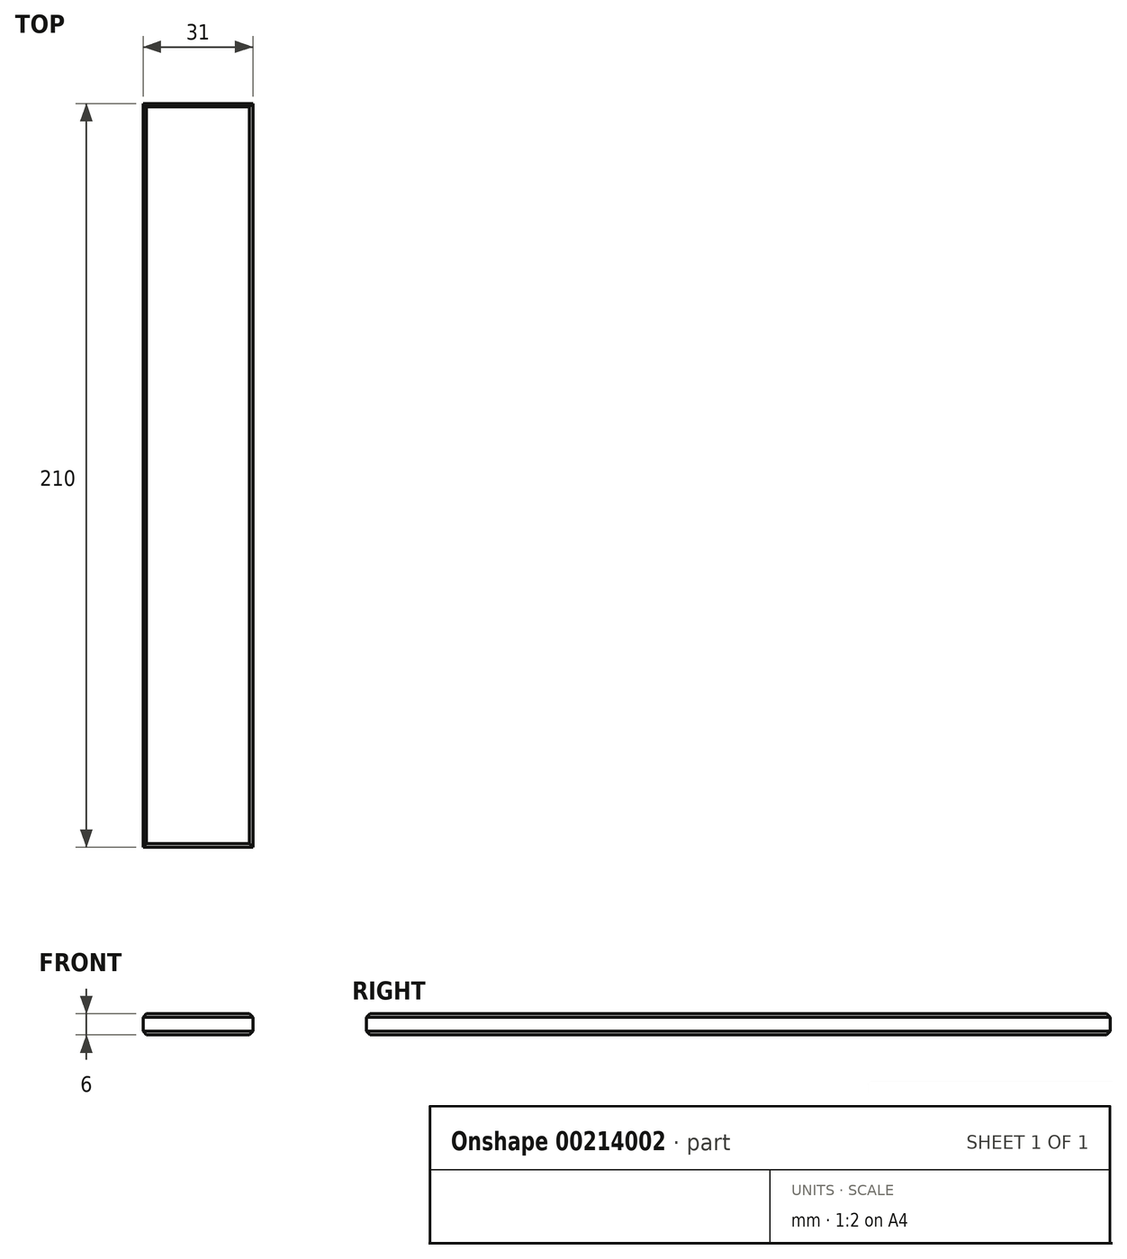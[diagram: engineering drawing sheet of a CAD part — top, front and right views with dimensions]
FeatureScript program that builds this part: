
annotation { "Feature Type Name" : "Feature", "Feature Type Description" : "" }
export const myFeature = defineFeature(function(context is Context, id is Id, definition is map)
    precondition{}
    {
        {
            var Q0;
            Q0=qCreatedBy(makeId("Top.planeOp"),FACE);
            var sketch = newSketch(context, id + "F0", { "sketchPlane" : qUnion([Q0])});
            skLineSegment(sketch, "E0.bottom", {"start": v(15.5, -105) * mm, "end": v(-15.5, -105) * mm});
            skLineSegment(sketch, "E0.top", {"start": v(15.5, 105) * mm, "end": v(-15.5, 105) * mm});
            skLineSegment(sketch, "E0.left", {"start": v(15.5, -105) * mm, "end": v(15.5, 105) * mm});
            skLineSegment(sketch, "E0.right", {"start": v(-15.5, -105) * mm, "end": v(-15.5, 105) * mm});
            skPoint(sketch, "E0.middle", {"position": v(0, 0) * mm});
            skSolve(sketch);
        }
        {
            var Q0;
            Q0=makeQuery(id+"F0.imprint","IMPRINT",FACE,{"disambiguationData":[TD([[makeQuery(id+"F0.imprint","IMPRINT",EDGE,{"derivedFrom":sQuery(id+"F0.wireOp",EDGE,"E0.bottom")}),-1.0]])]});
            extrude(context, id + "F1", {"entities" : qUnion([Q0]), "endBound" : BoundingType.SYMMETRIC, "depth" : 6 * mm});
        }
        {
            var Q0;
            Q0=makeQuery(id+"F1.opExtrude","CAP_EDGE",EDGE,{"disambiguationData":[OSD([sQuery(id+"F0.wireOp",EDGE,"E0.left")])],"isStart":false});
            var Q1;
            Q1=makeQuery(id+"F1.opExtrude","CAP_EDGE",EDGE,{"disambiguationData":[OSD([sQuery(id+"F0.wireOp",EDGE,"E0.top")])],"isStart":false});
            var Q2;
            Q2=makeQuery(id+"F1.opExtrude","CAP_EDGE",EDGE,{"disambiguationData":[OSD([sQuery(id+"F0.wireOp",EDGE,"E0.right")])],"isStart":false});
            var Q3;
            Q3=makeQuery(id+"F1.opExtrude","CAP_EDGE",EDGE,{"disambiguationData":[OSD([sQuery(id+"F0.wireOp",EDGE,"E0.bottom")])],"isStart":false});
            var Q4;
            Q4=makeQuery(id+"F1.opExtrude","CAP_EDGE",EDGE,{"disambiguationData":[OSD([sQuery(id+"F0.wireOp",EDGE,"E0.left")])],"isStart":true});
            var Q5;
            Q5=makeQuery(id+"F1.opExtrude","CAP_EDGE",EDGE,{"disambiguationData":[OSD([sQuery(id+"F0.wireOp",EDGE,"E0.right")])],"isStart":true});
            var Q6;
            Q6=makeQuery(id+"F1.opExtrude","CAP_EDGE",EDGE,{"disambiguationData":[OSD([sQuery(id+"F0.wireOp",EDGE,"E0.bottom")])],"isStart":true});
            var Q7;
            Q7=makeQuery(id+"F1.opExtrude","CAP_EDGE",EDGE,{"disambiguationData":[OSD([sQuery(id+"F0.wireOp",EDGE,"E0.top")])],"isStart":true});
            chamfer(context, id + "F2", {"entities" : qUnion([Q0, Q1, Q2, Q3, Q4, Q5, Q6, Q7]), "width" : 1 * mm, "tangentPropagation" : true});
        }
    });
